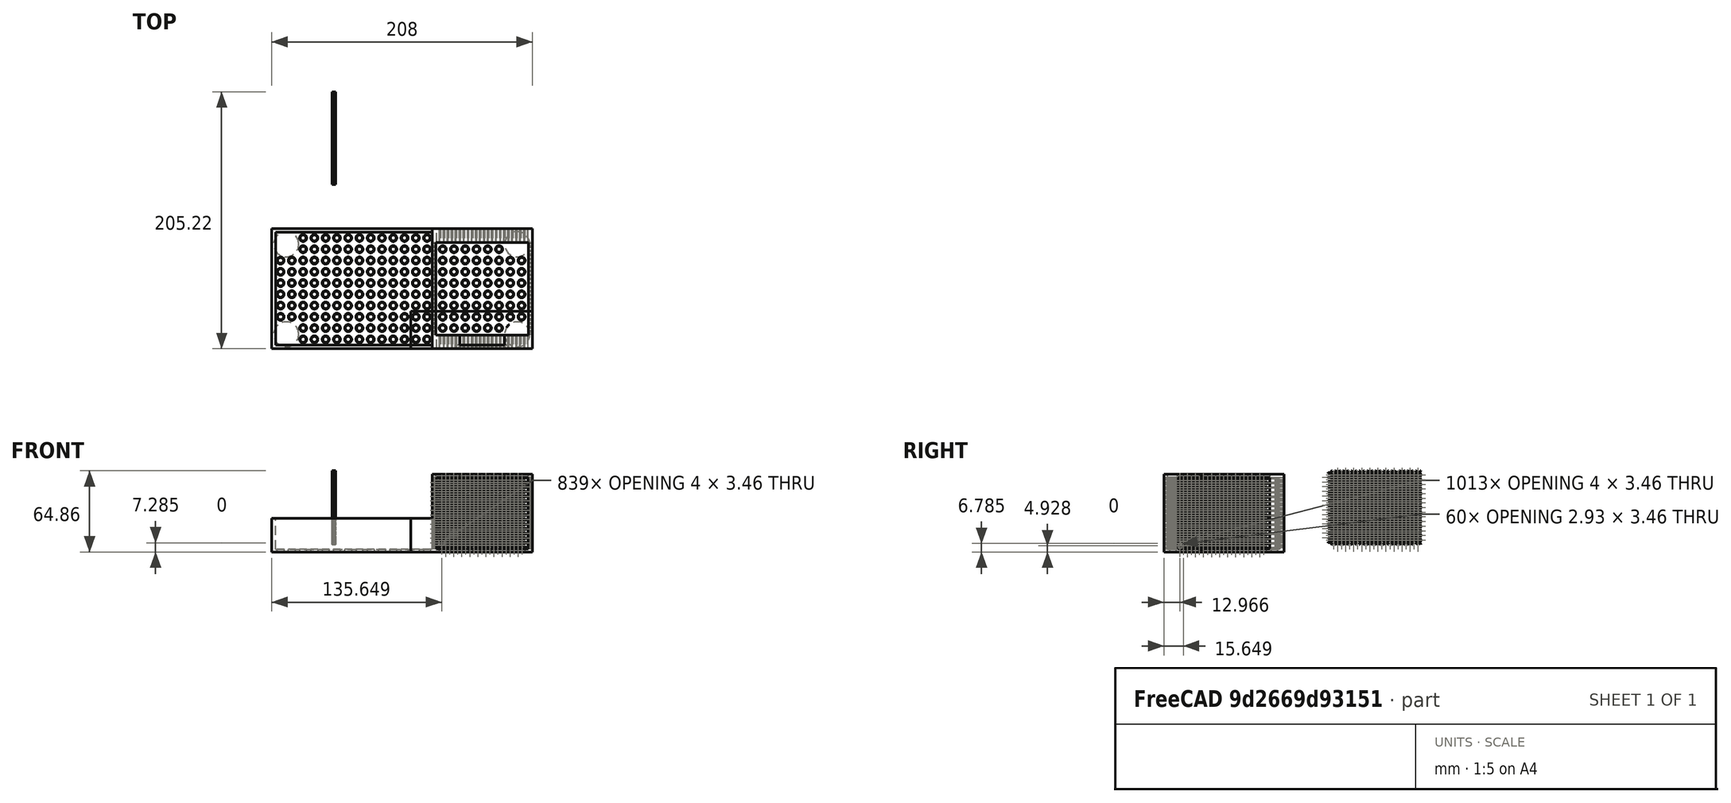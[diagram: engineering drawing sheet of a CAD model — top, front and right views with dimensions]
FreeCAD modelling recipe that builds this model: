
FCSTD DOCUMENT  (FreeCAD 0.18R4 (GitTag))
Label: esponja_jabon
License: All rights reserved
LicenseURL: http://en.wikipedia.org/wiki/All_rights_reserved
objects: Part::Box×16, Part::Cut×16, Part::Cylinder×8, Part::MultiFuse×6, Part::Feature×5, Part::FeaturePython×4, Part::Cone×2, Spreadsheet::Sheet×1, Part::RegularPolygon×1, Part::Extrusion×1, Mesh::Feature×1
note: 59 computed .brp shape members not serialized (recipe doc carries the construction recipe); baked Part::Feature solids carry a one-line shape summary decoded from their .brp

FEATURE [Part::Box] Box  label="Cube"
  AttacherType = Attacher::AttachEngine3D
  Height = 27
  Length = 128
  Width = 96
FEATURE [Part::Box] Box001  label="Cube001"
  AttacherType = Attacher::AttachEngine3D
  Height = 62
  Length = 125
  Placement = pos=(3,3,2) rot=(0,0,1;0rad)
  Width = 90
FEATURE [Part::Cut] Cut
  Base = -> Box
  Refine = true
  Tool = -> Box001
FEATURE [Part::Box] Box002  label="Cube002"
  AttacherType = Attacher::AttachEngine3D
  Height = 62
  Length = 80
  Placement = pos=(128,0,0) rot=(0,0,1;0rad)
  Width = 96
FEATURE [Part::Box] Box003  label="Cube003"
  AttacherType = Attacher::AttachEngine3D
  Height = 60
  Length = 74
  Placement = pos=(131,11,2) rot=(0,0,1;0rad)
  Width = 74
FEATURE [Part::Cone] Cone007  label="Cone001"
  Angle = 360
  AttacherType = Attacher::AttachEngine3D
  Height = 3
  Placement = pos=(7,7,0) rot=(0,0,1;0rad)
  Radius1 = 3
  Radius2 = 2.17
FEATURE [Part::Cone] Cone008
  Angle = 360
  AttacherType = Attacher::AttachEngine3D
  Height = 3
  Placement = pos=(135,16,0) rot=(0,0,1;0rad)
  Radius1 = 3
  Radius2 = 2.17
FEATURE [Part::Cylinder] Cylinder  label="Cylinder_up_left_add"
  Angle = 360
  AttacherType = Attacher::AttachEngine3D
  Height = 2
  Placement = pos=(11.5,11.5,0) rot=(0,0,1;0rad)
  Radius = 10
FEATURE [Part::Cylinder] Cylinder001  label="Cylinder001_down_left_add"
  Angle = 360
  AttacherType = Attacher::AttachEngine3D
  Height = 2
  Placement = pos=(11.5,83.5,0) rot=(0,0,1;0rad)
  Radius = 10
FEATURE [Part::Cylinder] Cylinder002  label="Cylinder002_up_right_Add"
  Angle = 360
  AttacherType = Attacher::AttachEngine3D
  Height = 2
  Placement = pos=(196,11.5,0) rot=(0,0,1;0rad)
  Radius = 10
FEATURE [Part::Cylinder] Cylinder003  label="Cylinder003_down_right_add"
  Angle = 360
  AttacherType = Attacher::AttachEngine3D
  Height = 2
  Placement = pos=(196,83.5,0) rot=(0,0,1;0rad)
  Radius = 10
FEATURE [Part::Cylinder] Cylinder004  label="Cylinder_up_left001_minus"
  Angle = 360
  AttacherType = Attacher::AttachEngine3D
  Height = 2
  Placement = pos=(11.5,11.5,-1.75) rot=(0,0,1;0rad)
  Radius = 10
FEATURE [Part::Cylinder] Cylinder005  label="Cylinder001_down_left001_minus"
  Angle = 360
  AttacherType = Attacher::AttachEngine3D
  Height = 2
  Placement = pos=(11.5,83.5,-1.75) rot=(0,0,1;0rad)
  Radius = 10
FEATURE [Part::Cylinder] Cylinder006  label="Cylinder002_up_right001_minus"
  Angle = 360
  AttacherType = Attacher::AttachEngine3D
  Height = 2
  Placement = pos=(196,11.5,-1.75) rot=(0,0,1;0rad)
  Radius = 10
FEATURE [Part::Cylinder] Cylinder007  label="Cylinder003_down_right001_minus"
  Angle = 360
  AttacherType = Attacher::AttachEngine3D
  Height = 2
  Placement = pos=(196,83.5,-1.75) rot=(0,0,1;0rad)
  Radius = 10
FEATURE [Spreadsheet::Sheet] EditMe
  cells = A1=User Variables; D1=Calculated Values; A2=Hexagon Radius:; B2(radius)=2; D2=X Interval:; E2(xInterval)==2 * sin(60deg) * (B2 * 2 + B3 - 0.267949 * B2); A3=Hexagon Separation:; B3(separation)=0.25; D3=Y Interval:; E3(yInterval)==2 * B2 + B3 - 0.267949 * B2; A4=Grid Width:; B4(width)=59; D4=First X:; E4(firstX)==B2; A5=Grid Length:; B5(length)=74; D5=First Y:; E5(firstY)==B2; A6=Grid Height:; B6(height)=3; D6=Count X:; E6(countX)==round(B5 / E2) + 2; D7=Count Y:; E7(countY)==round(B4 / E3) + 2; A8=Tweak X:; B8(tweakX)=0; D8=Array2 XPos:; E8(array2XPos)==sin(60deg) * (B2 * 2 + B3 - 0.267949 * B2); A9=Tweak Y:; B9(tweakY)=0; D9=Array2 YPos:; E9(array2YPos)==E3 / 2; A10=Tweak Z:; B10(tweakZ)=0; A11=Instructions:\n\nYou should only run the macro once unless you want to start again from scratch.\n\nEdit the values in column B to define your honeycomb.  You can also edit the objects (plate, arrays, etc.), but it's \nprobably better to do all the editing here in the spreadsheet at least until you get it more or less like you want it before\ndoing some final tweaking directly on the objects.\n\nHexagon radius -- the circumradius of the individual hexagons (circle with each vertex on its circumference).\n\nHexagon separation -- distance between each hexagon, the thickness of the grid produced after cutting the hexagons from the plate.\n\nPlate dimensions -- sets the dimensions of the plate out of which the honeycomb can be cut.  These values are used to calculate\nthe countX and countY variables.  You can delete the plate object if you wish to apply the hexagon arrays to a different structure.\n\nTweak X,Y,Z -- Edit these to move both hexagon arrays independently of the plate object, for example to center the arrays inside \nthe plate.\n\nCountX and CountY -- number of hexagons in the 2 arrays.  These are calculated based on the plate size, radius of hexagons, and \nseparation between them, but you will probably want to modify these manually.  Just remember if you modify them you are replacing \nthe formulas in those cells with immediate values, and thus they won't be recalulated for you if other changes are made.\n\nIf you would prefer a round plate, simply delete the plate object and replace it with a cylinder, and then use the Tweak values \nand countX and countY variables to arrange the hexagon arrays to your liking.
FEATURE [Part::RegularPolygon] HoneycombHexagon
  AttacherType = Attacher::AttachEngine3D
  Circumradius = 2
  Polygon = 6
  expr: Circumradius = EditMe.radius
FEATURE [Part::Extrusion] ExtrudedHexagon
  Base = -> HoneycombHexagon
  Dir = (0,0,1)
  DirMode = 0
  FaceMakerClass = Part::FaceMakerBullseye
  LengthFwd = 3
  LengthRev = 0
  Placement = pos=(2,2,0) rot=(0,0,1;0rad)
  Solid = true
  Symmetric = false
  expr: Placement.Base.z = EditMe.tweakZ
  expr: Placement.Base.y = EditMe.firstY + EditMe.tweakY
  expr: Placement.Base.x = EditMe.firstX + EditMe.tweakX
  expr: LengthFwd = EditMe.height
FEATURE [Part::FeaturePython] HoneycombArray1  # Draft array (typed FeaturePython)
  Angle = 360
  ArrayType = 0
  Axis = (0,0,1)
  Base = -> ExtrudedHexagon
  Center = (0,0,0)
  Fuse = false
  IntervalAxis = (0,0,0)
  IntervalX = (6.43301,0,0)
  IntervalY = (0,3.7141,0)
  IntervalZ = (0,0,1)
  NumberPolar = 1
  NumberX = 14
  NumberY = 18
  NumberZ = 1
  expr: NumberY = EditMe.countY
  expr: NumberX = EditMe.countX
  expr: IntervalY.y = EditMe.yInterval
  expr: IntervalX.x = EditMe.xInterval
FEATURE [Part::FeaturePython] HoneycombArray2  # Draft array (typed FeaturePython)
  Angle = 360
  ArrayType = 0
  Axis = (0,0,1)
  Base = -> ExtrudedHexagon
  Center = (0,0,0)
  Fuse = false
  IntervalAxis = (0,0,0)
  IntervalX = (6.43301,0,0)
  IntervalY = (0,3.7141,0)
  IntervalZ = (0,0,1)
  NumberPolar = 1
  NumberX = 14
  NumberY = 18
  NumberZ = 1
  Placement = pos=(3.21651,1.85705,0) rot=(0,0,1;0rad)
  expr: NumberY = EditMe.countY
  expr: NumberX = EditMe.countX
  expr: IntervalY.y = EditMe.yInterval
  expr: IntervalX.x = EditMe.xInterval
  expr: Placement.Base.y = EditMe.array2YPos
  expr: Placement.Base.x = EditMe.array2XPos
FEATURE [Part::MultiFuse] Fused_Arrays
  Refine = true
  Shapes = -> [HoneycombArray1,HoneycombArray2]
FEATURE [Part::Box] Plate
  AttacherType = Attacher::AttachEngine3D
  Height = 3
  Length = 74
  Placement = pos=(7.21651,5.85705,0) rot=(0,0,1;0rad)
  Width = 59
  expr: Placement.Base.y = EditMe.array2YPos + EditMe.radius * 2
  expr: Placement.Base.x = EditMe.array2XPos + EditMe.radius * 2
  expr: Height = EditMe.height
  expr: Width = EditMe.width
  expr: Length = EditMe.length
FEATURE [Part::Cut] HoneycombGrid
  Base = -> Plate
  Placement = pos=(48,124,0) rot=(0.57735,0.57735,0.57735;2.0944rad)
  Refine = true
  Tool = -> Fused_Arrays
FEATURE [Part::Box] Box012  label="Cube012"
  AttacherType = Attacher::AttachEngine3D
  Height = 57
  Length = 73
  Placement = pos=(131.5,-0.5,2.5) rot=(0,0,1;0rad)
  Width = 12
FEATURE [Part::Box] Box014  label="Cube014"
  AttacherType = Attacher::AttachEngine3D
  Height = 57
  Length = 73
  Placement = pos=(209,11.5,2.5) rot=(0,0,1;1.5708rad)
  Width = 5
FEATURE [Part::Box] Box015  label="Cube015"
  AttacherType = Attacher::AttachEngine3D
  Height = 57
  Length = 73
  Placement = pos=(132,11.5,2.5) rot=(0,0,1;1.5708rad)
  Width = 5
FEATURE [Part::Cut] Cut001
  Base = -> Box002
  Refine = true
  Tool = -> Box003
FEATURE [Part::MultiFuse] Fusion
  Refine = true
  Shapes = -> [Cut,Cut001]
FEATURE [Part::Box] Box018  label="Cube018"
  AttacherType = Attacher::AttachEngine3D
  Height = 57
  Length = 73
  Placement = pos=(131.5,84.5,2.5) rot=(0,0,1;0rad)
  Width = 12
FEATURE [Part::Cut] Cut002
  Base = -> Fusion
  Refine = true
  Tool = -> Box018
FEATURE [Part::Cut] Cut003
  Base = -> Cut002
  Refine = true
  Tool = -> Box012
FEATURE [Part::Cut] Cut004
  Base = -> Cut003
  Refine = true
  Tool = -> Box014
FEATURE [Part::Cut] Cut005  label="pieza_sin_panel_sin_agujeros"
  Base = -> Cut004
  Refine = true
  Tool = -> Box015
FEATURE [Part::FeaturePython] Array  # Draft array (typed FeaturePython)
  Angle = 360
  ArrayType = 0
  Axis = (0,0,1)
  Base = -> Cone007
  Center = (0,0,0)
  Fuse = false
  IntervalAxis = (0,0,0)
  IntervalX = (9,0,0)
  IntervalY = (0,9,0)
  IntervalZ = (0,0,1)
  NumberPolar = 1
  NumberX = 14
  NumberY = 10
  NumberZ = 1
  Placement = pos=(0,95.5,2.5) rot=(1,0,0;3.14159rad)
FEATURE [Part::FeaturePython] Array001  # Draft array (typed FeaturePython)
  Angle = 360
  ArrayType = 0
  Axis = (0,0,1)
  Base = -> Cone008
  Center = (0,0,0)
  Fuse = false
  IntervalAxis = (0,0,0)
  IntervalX = (9,0,0)
  IntervalY = (0,9,0)
  IntervalZ = (0,0,1)
  NumberPolar = 1
  NumberX = 8
  NumberY = 8
  NumberZ = 1
  Placement = pos=(1.5,95.5,2.5) rot=(1,0,0;3.14159rad)
FEATURE [Part::Feature] HoneycombGrid001  label="HoneycombGrid_lateral1"
  Placement = pos=(124,11,-4) rot=(1,0,0;1.5708rad)
  shape: bbox 74 x 11 x 59 mm, 2299 faces (baked)
FEATURE [Part::Feature] HoneycombGrid003  label="HoneycombGrid_frente"
  Placement = pos=(205,4,-4.5) rot=(0.57735,0.57735,0.57735;2.0944rad)
  shape: bbox 3 x 74 x 59 mm, 2299 faces (baked)
FEATURE [Part::Feature] HoneycombGrid005  label="HoneycombGrid_lateral2"
  Placement = pos=(124,96,-4) rot=(1,0,0;1.5708rad)
  shape: bbox 74 x 11 x 59 mm, 2299 faces (baked)
FEATURE [Part::Feature] HoneycombGrid006  label="HoneycombGrid_fondo"
  Placement = pos=(128,4,-4.5) rot=(0.57735,0.57735,0.57735;2.0944rad)
  shape: bbox 3 x 74 x 59 mm, 2299 faces (baked)
FEATURE [Part::Cut] Cut006
  Base = -> Cut005
  Refine = true
  Tool = -> Array001
FEATURE [Part::Cut] Cut007  label="pieza_con_agujeros_base_sin_apoyos"
  Base = -> Cut006
  Refine = true
  Tool = -> Array
FEATURE [Part::MultiFuse] Fusion001
  Refine = true
  Shapes = -> [Cut007,Cylinder,Cylinder001,Cylinder002,Cylinder003]
FEATURE [Part::Cut] Cut008
  Base = -> Fusion001
  Refine = true
  Tool = -> Cylinder007
FEATURE [Part::Cut] Cut009
  Base = -> Cut008
  Refine = true
  Tool = -> Cylinder006
FEATURE [Part::Cut] Cut010
  Base = -> Cut009
  Refine = true
  Tool = -> Cylinder005
FEATURE [Part::Cut] Cut011  label="pieza_agujeros_no_panal_con_bases"
  Base = -> Cut010
  Refine = true
  Tool = -> Cylinder004
FEATURE [Part::MultiFuse] Fusion002  label="jabonera"
  Refine = true
  Shapes = -> [Cut011,HoneycombGrid003,HoneycombGrid001,HoneycombGrid006,HoneycombGrid005]
FEATURE [Part::Feature] Fusion002001  label="jabonera001"
  shape: bbox 208 x 96 x 62 mm, 9343 faces (baked)
FEATURE [Part::Box] Box019  label="Cube019"
  AttacherType = Attacher::AttachEngine3D
  Height = 70
  Length = 124
  Placement = pos=(-13,-9,0) rot=(0,0,1;0rad)
  Width = 124
FEATURE [Part::Cut] Cut012
  Base = -> Fusion002001
  Refine = true
  Tool = -> Box019
FEATURE [Part::Box] Box020  label="Cube020"
  AttacherType = Attacher::AttachEngine3D
  Height = 73
  Length = 100
  Placement = pos=(110,30,0) rot=(0,0,1;0rad)
  Width = 110
FEATURE [Part::Cut] Cut013
  Base = -> Cut012
  Refine = true
  Tool = -> Box020
FEATURE [Part::Box] Box021  label="Cube021"
  AttacherType = Attacher::AttachEngine3D
  Height = 60
  Length = 3
  Placement = pos=(205,27,0) rot=(0,0,1;0rad)
  Width = 3
FEATURE [Part::Box] Box022  label="Cube022"
  AttacherType = Attacher::AttachEngine3D
  Height = 60
  Length = 3
  Placement = pos=(128,27,0) rot=(0,0,1;0rad)
  Width = 3
FEATURE [Part::MultiFuse] Fusion002002  label="test_jabonera"
  Refine = true
  Shapes = -> [Cut013,Box022,Box021]
FEATURE [Part::Box] Box023  label="Cube023"
  AttacherType = Attacher::AttachEngine3D
  Height = 96
  Length = 36
  Placement = pos=(150,3,2) rot=(0,0,1;0rad)
  Width = 54
FEATURE [Part::Cut] Cut014
  Base = -> Fusion002002
  Refine = true
  Tool = -> Box023
FEATURE [Part::Box] Box024  label="Cube024"
  AttacherType = Attacher::AttachEngine3D
  Height = 60
  Length = 3
  Placement = pos=(147,3,2) rot=(0,0,1;0rad)
  Width = 8
FEATURE [Part::Box] Box025  label="Cube025"
  AttacherType = Attacher::AttachEngine3D
  Height = 60
  Length = 3
  Placement = pos=(186,3,2) rot=(0,0,1;0rad)
  Width = 8
FEATURE [Part::MultiFuse] Fusion002003  label="tes_jabonera_min"
  Refine = true
  Shapes = -> [Cut014,Box025,Box024]
FEATURE [Mesh::Feature] Mesh  label="tes_jabonera_min (Meshed)"
